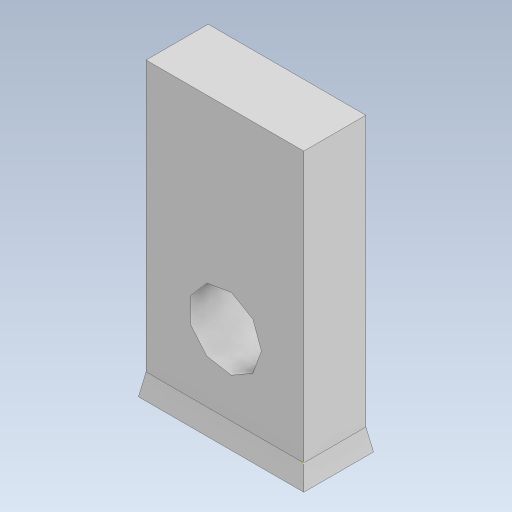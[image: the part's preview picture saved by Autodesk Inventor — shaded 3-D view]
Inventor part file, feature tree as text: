
AUTODESK INVENTOR PART (.ipt)
format: ipt  version: 2023 (Build 270158000, 158)  size: 102,400 bytes
history: native  units: in
note: dims shown in document units (in); Inventor stores cm internally (conversion verified against a paired STEP export)
features: sketch x3, extrude x1, hole x1
ambient origin geometry x8: Origin, YZ Plane, XZ Plane, XY Plane, X Axis, Y Axis, Z Axis, Center Point
bodies: Solid1 (feature_tree)
feature tree (5):
  sketch  "Sketch1"  dims[d0=0.5748in d1=0.2264in]
  extrude  "Extrusion1"  Depth=0.2264in
  hole  "Hole1"  [1 undecoded]
  sketch  "Sketch2"  dims[d2=0.9843in d3=0.0787in d4=0.0in d5=0.0687in d6=0.7087in]
  sketch  "Sketch3"  dims[d7=0.266in d8=0.2362in d9=0.507in d10=0.0787in d11=0.5635in d12=0.5in d13=0.8108in]
note: 1 required parameter value undecoded (feature->parameter linkage not recoverable at this tier; creation-order binding heuristic only, values carry confidence <= 0.55)
